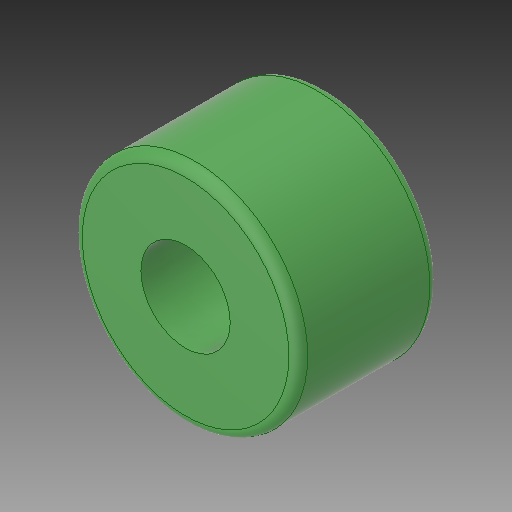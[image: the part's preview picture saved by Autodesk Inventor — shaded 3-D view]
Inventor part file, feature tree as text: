
AUTODESK INVENTOR PART (.ipt)
format: ipt  version: 2019.3 (Build 233278000, 278)  size: 140,800 bytes
history: native  units: mm
features: other x1, extrude x1, fillet x1, sketch x1
ambient origin geometry x8: Origin, YZ Plane, XZ Plane, XY Plane, X Axis, Y Axis, Z Axis, Center Point
bodies: Body1 (feature_tree)
feature tree (4):
  other  "Твердое тело1"
  extrude  "Выдавливание1"  Depth=24.0mm
  fillet  "Сопряжение1"  Radius=9.5mm
  sketch  "Эскиз1"
